# Revit family: HARMANN-SENSOVENT DUCT EC_Wywiewny
name_source: partatom
category: Wyposażenie mechaniczne
units: mm (PartAtom-declared; Revit-internal decimal feet)

## family parameters
Oparty na płaszczyźnie roboczej = Nie
Punkt obliczania pomieszczeń = Nie
Tnij formami wycięć po wczytaniu = Nie
Typ części = Dzieli na
Współdzielony = Nie
Wymiar okrągłego złącza = Użyj średnicy
Zachowaj orientację opisów = Nie
Zawsze pionowo = Tak

## types (6) — shared parameters
Domyślna rzędna = 0.0 mm
IfcExportAs = IfcFanType
IfcExportType = NOTDEFINED
Kod Producent = Harmann
Kod Typoszereg = SENSOVENT DUCT EC
Object Date = 2018.11.30
Object Destination = PL
Object ID = F000054RFAPL
Object Language = PL
Object Revit = 2017
Object Version = 1.00
Otoczenie Temperatura Maksymalna = 50.0 °C
Otoczenie Temperatura Minimalna = -20.0 °C
Powietrze Wywiewane Temperatura Maksymalna = 50.0 °C
Producent = Harmann Polska Sp. z o.o.
Producent Nazwa = Harmann Polska Sp. z o.o.
Systematyka Branża = Instalacje Sanitarne
Systematyka Dziedzina = Instalacje Wentylacyjne
Systematyka Klasa = Wentylator
Systematyka Rodzaj = Wentylator Kanałowy
Zasilanie Częstotliwość Nominalna = 50 Hz
Zasilanie Ilość Faz = 1
Zasilanie Konfiguracja Uzwojeń = n/d
Zasilanie Napięcie Nominalne = 230 V
Zasilanie Rodzaj Sterowania = Sterowanie napięciem 0-10V. Wbudowany regulator ciśnienia.
wx_a0 = 0.0 mm
wy_a0 = 53.9 mm

## per-type parameters (varying)
| type | Kod Numer Katalogowy | Masa Netto | Opis | Otoczenie Poziom Ciśnienia Akustycznego Nominalny z 01 m | Otoczenie Poziom Ciśnienia Akustycznego Nominalny z 03 m | Otoczenie Poziom Mocy Akustycznej Nominalny Obudowa | Powietrze Wywiewane Ciśnienie Statyczne Maksymalne | Powietrze Wywiewane Ciśnienie Statyczne Nominalne | Powietrze Wywiewane Poziom Mocy Akustycznej Nominalny Wlot | Powietrze Wywiewane Poziom Mocy Akustycznej Nominalny Wylot | Powietrze Wywiewane Przepływ Maksymalny | Powietrze Wywiewane Przepływ Nominalny | Prt Komponent N1 | Prt Komponent N2 | Zasilanie Moc | Zasilanie Moc Pozorna | Zasilanie Natężenie | Zasilanie Współczynnik Mocy | dn | l1_a0 | l2_a0 | s1 | wz_a0 |
| SENSOVENT DUCT 10 EC | 05002000 | 2.0 kg | Kanałowy wentylator  EC | 38 | 35 | 42 | 160.0 Pa | 60.0 Pa | 52 | 53 | 280 m³/h | 150 m³/h | GE-Komponent-ParaForma-Harmann-ML-N1a : DUCT 10 EC | GE-Komponent-ParaForma-Harmann-ML-N2a : 10 EC | 20 W | 58 VA | 0 A | 0.35 | 100.0 mm | 119.0 mm | 119.0 mm | 100.0 mm | 88.5 mm |
| SENSOVENT DUCT 12 EC | 05002001 | 1.8 kg | Kanałowy wentylator  EC | 37 | 34 | 41 | 140.0 Pa | 50.0 Pa | 55 | 55 | 300 m³/h | 200 m³/h | GE-Komponent-ParaForma-Harmann-ML-N1a : DUCT 12 EC | GE-Komponent-ParaForma-Harmann-ML-N2a : 12 EC | 18 W | 61 VA | 0 A | 0.21 | 125.0 mm | 99.5 mm | 99.5 mm | 125.0 mm | 88.5 mm |
| SENSOVENT DUCT 15/16 EC | 05002002 | 2.7 kg | Kanałowy wentylator  EC | 439 | 36 | 43 | 350.0 Pa | 80.0 Pa | 55 | 58 | 530 m³/h | 350 m³/h | GE-Komponent-ParaForma-Harmann-ML-N1a : DUCT 15-16 EC | GE-Komponent-ParaForma-Harmann-ML-N2a : 15-16 EC | 50 W | 80 VA | 0 A | 0.62 | 160.0 mm | 145.0 mm | 145.0 mm | 160.0 mm | 99.5 mm |
| SENSOVENT DUCT 20 EC | 05002003 | 4.3 kg | Kanałowy wentylator EC | 44 | 41 | 48 | 450.0 Pa | 100.0 Pa | 60 | 62 | 1100 m³/h | 700 m³/h | GE-Komponent-ParaForma-Harmann-ML-N1a : DUCT 20 EC | GE-Komponent-ParaForma-Harmann-ML-N2a : 20 EC | 165 W | 241 VA | 1 A | 0.68 | 200.0 mm | 120.0 mm | 120.0 mm | 200.0 mm | 111.0 mm |
| SENSOVENT DUCT 25 EC | 05002004 | 6.5 kg | Kanałowy wentylator EC | 47 | 44 | 51 | 600.0 Pa | 120.0 Pa | 59 | 60 | 1600 m³/h | 900 m³/h | GE-Komponent-ParaForma-Harmann-ML-N1a : DUCT 25 EC | GE-Komponent-ParaForma-Harmann-ML-N2a : 25 EC | 255 W | 614 VA | 3 A | 0.42 | 250.0 mm | 159.5 mm | 159.5 mm | 250.0 mm | 111.0 mm |
| SENSOVENT DUCT 31 EC | 05002005 | 8.5 kg | Kanałowy wentylator EC | 50 | 47 | 54 | 700.0 Pa | 150.0 Pa | 61 | 64 | 2100 m³/h | 1000 m³/h | GE-Komponent-ParaForma-Harmann-ML-N1a : DUCT 31 EC | GE-Komponent-ParaForma-Harmann-ML-N2a : 31  EC | 254 W | 621 VA | 3 A | 0.41 | 315.0 mm | 177.0 mm | 177.0 mm | 315.0 mm | 157.5 mm |

note: column(s) folded — value = type name in every type: Kod Zamówienia, Model, Opis indeksowy
